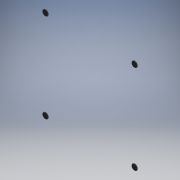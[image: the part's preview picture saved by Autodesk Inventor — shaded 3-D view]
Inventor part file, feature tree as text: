
AUTODESK INVENTOR PART (.ipt)
format: ipt  version: 2018 (Build 220112000, 112)  size: 113,664 bytes
history: native  units: in
note: dims shown in document units (in); Inventor stores cm internally (conversion verified against a paired STEP export)
features: reference x4, projected_geometry x4, other x3, extrude x2, sketch x2, fillet x1
ambient origin geometry x8: Origin, YZ Plane, XZ Plane, XY Plane, X Axis, Y Axis, Z Axis, Center Point
bodies: Solid1 (feature_tree)
feature tree (16):
  extrude  "Extrusion1"  Depth=0.01in TaperAngle=0.0deg
  extrude  "Extrusion2"  [1 undecoded]
  fillet  "Fillet1"  [1 undecoded]
  sketch  "Sketch1"  dims[d0=0.01in d1=0.0in d2=0.01in d3=0.0in]
  reference  "Reference1"
  reference  "Reference2"
  reference  "Reference3"
  reference  "Reference4"
  sketch  "Sketch2"  dims[d4=0.01in]
  projected_geometry  "Projected Loop1"
  projected_geometry  "Projected Loop2"
  projected_geometry  "Projected Loop3"
  projected_geometry  "Projected Loop4"
  other  "<userpath>\Documents\Commodore Cube Project\Case\Assembly.iam"
  other  "Assembly.iam"
  other  "Tray:1"
note: 2 required parameter values undecoded (feature->parameter linkage not recoverable at this tier; creation-order binding heuristic only, values carry confidence <= 0.55)
